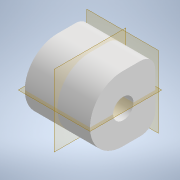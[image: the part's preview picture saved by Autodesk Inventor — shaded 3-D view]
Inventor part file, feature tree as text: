
AUTODESK INVENTOR PART (.ipt)
format: ipt  version: 2021 (Build 250183000, 183)  size: 120,832 bytes
history: native  units: mm
features: extrude x2, fillet x2, sketch x2
ambient origin geometry x8: Origin, YZ Plane, XZ Plane, XY Plane, X Axis, Y Axis, Z Axis, Center Point
bodies: Body1 (feature_tree)
feature tree (6):
  extrude  "Wyciągnięcie proste3"  Depth=80.0mm
  fillet  "Zaokrąglenie2"  Radius=80.0mm
  fillet  "Zaokrąglenie3"  Radius=80.0mm
  extrude  "Wyciągnięcie proste4"  Depth=18.0mm
  sketch  "Szkic3"
  sketch  "Szkic4"
